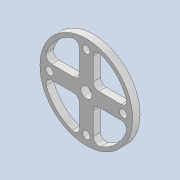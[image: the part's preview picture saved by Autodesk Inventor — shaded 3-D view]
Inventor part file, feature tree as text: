
AUTODESK INVENTOR PART (.ipt)
format: ipt  version: 2020 (Build 240168000, 168)  size: 222,720 bytes
history: native  units: mm
features: other x4, extrude x3, sketch x3, fillet x1, reference x1
ambient origin geometry x8: Origin, YZ Plane, XZ Plane, XY Plane, X Axis, Y Axis, Z Axis, Center Point
bodies: Solid1 (feature_tree)
feature tree (12):
  extrude  "Extrusion1"  Depth=8.0mm
  extrude  "Extrusion2"  Depth=4.0mm
  extrude  "Extrusion3"  Depth=0.5mm TaperAngle=0.0deg
  fillet  "Fillet1"  Radius=0.5mm
  sketch  "Sketch1"  dims[d0=2.0mm d1=0.0mm d2=8.0mm]
  reference  "Reference1"
  sketch  "Sketch2"  dims[d3=6.0mm d4=0.0mm d5=4.0mm]
  sketch  "Sketch3"  dims[d6=0.5mm d7=6.0mm d8=0.0mm d9=0.5mm]
  parser-record x1  (decoder bookkeeping rows leaked as tree rows — omitted from the tree; the rows remain in map.json)
  other  "tip_3_n_base_ass.iam"
  other  "mot_27_ass:2"
  other  "mot_27_1:1"
note: 1 file-system path scrubbed to <path> (originals preserved in map.json)
